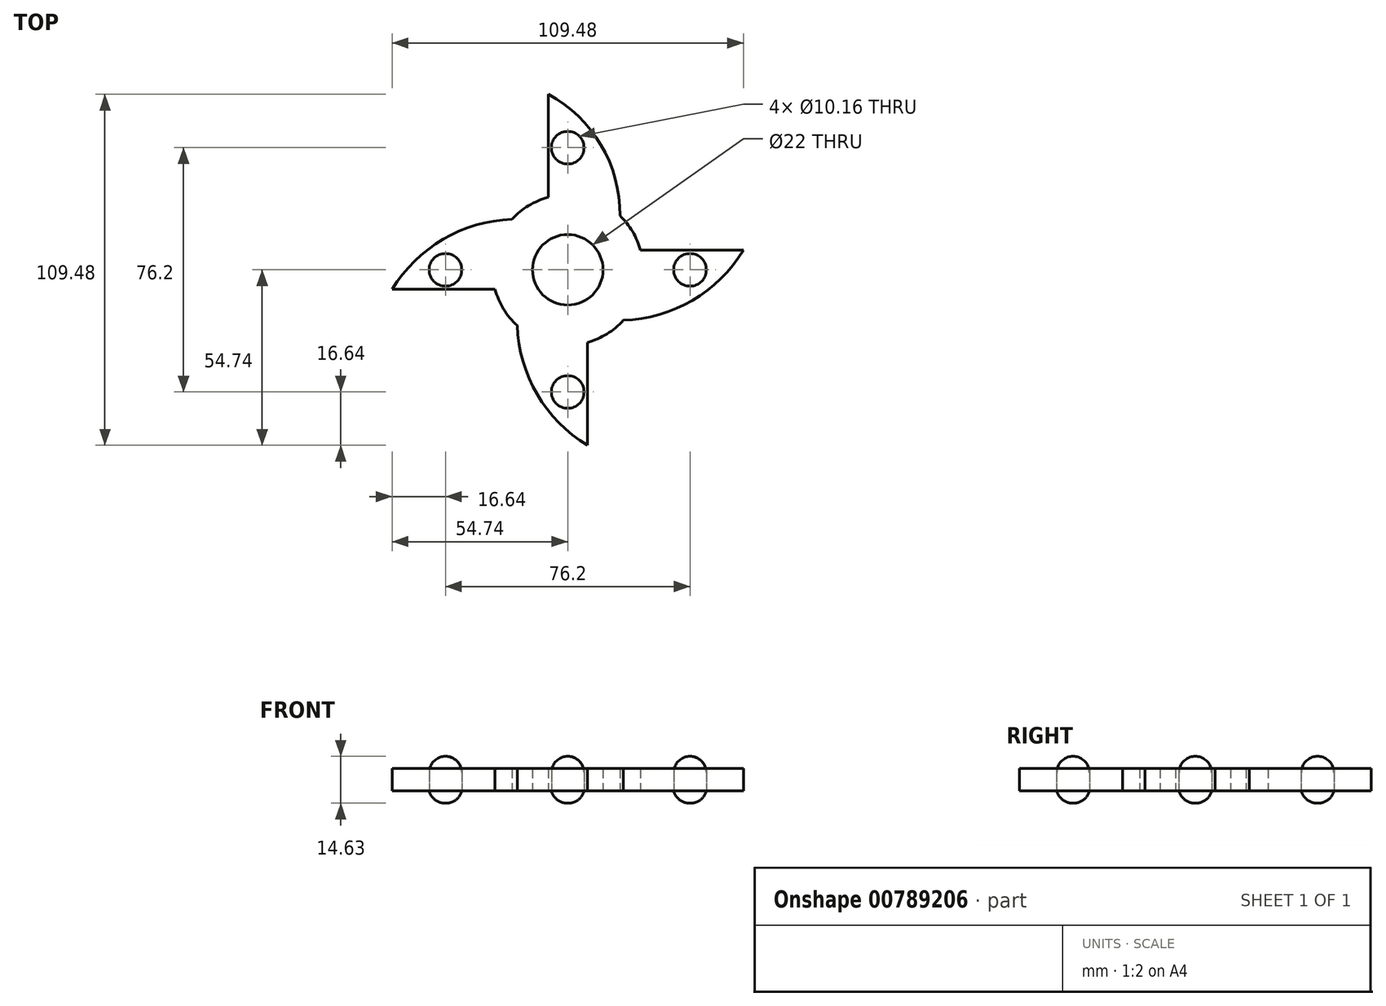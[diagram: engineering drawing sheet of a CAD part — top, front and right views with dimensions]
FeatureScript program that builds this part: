
annotation { "Feature Type Name" : "Feature", "Feature Type Description" : "" }
export const myFeature = defineFeature(function(context is Context, id is Id, definition is map)
    precondition{}
    {
        {
            var Q0;
            Q0=qCreatedBy(makeId("Top.planeOp"),FACE);
            var sketch = newSketch(context, id + "F0", { "sketchPlane" : qUnion([Q0])});
            skCircle(sketch, "E0", {"center": v(0, 0) * mm, "radius": 11 * mm});
            skCircle(sketch, "E1", {"center": v(0, 0) * mm, "radius": 4 * mm});
            skCircle(sketch, "E2", {"center": v(0, 0) * mm, "radius": 12.5 * mm});
            skCircle(sketch, "E3.cCircle", {"center": v(0, 0) * mm, "radius": 12.5 * mm, "construction": true});
            skCircle(sketch, "E4.cCircle", {"center": v(0, 0) * mm, "radius": 14.74 * mm, "construction": true});
            skLineSegment(sketch, "E4.0", {"start": v(6.1, -14.74) * mm, "end": v(-6.1, -14.74) * mm});
            skLineSegment(sketch, "E4.1", {"start": v(-6.1, -14.74) * mm, "end": v(-14.74, -6.1) * mm});
            skLineSegment(sketch, "E4.2", {"start": v(-14.74, -6.1) * mm, "end": v(-14.74, 6.1) * mm});
            skLineSegment(sketch, "E4.3", {"start": v(-14.74, 6.1) * mm, "end": v(-6.1, 14.74) * mm});
            skLineSegment(sketch, "E4.4", {"start": v(-6.1, 14.74) * mm, "end": v(6.1, 14.74) * mm});
            skLineSegment(sketch, "E4.5", {"start": v(6.1, 14.74) * mm, "end": v(14.74, 6.1) * mm});
            skLineSegment(sketch, "E4.6", {"start": v(14.74, 6.1) * mm, "end": v(14.74, -6.1) * mm});
            skLineSegment(sketch, "E4.7", {"start": v(14.74, -6.1) * mm, "end": v(6.1, -14.74) * mm});
            skPoint(sketch, "E4.0.midPoint", {"position": v(0, -14.74) * mm});
            skLineSegment(sketch, "E5", {"start": v(-6.1, 14.74) * mm, "end": v(-6.1, 54.74) * mm});
            skLineSegment(sketch, "E6", {"start": v(6.1, 14.74) * mm, "end": v(15.92, 22.8) * mm});
            skArc(sketch, "E7", {"start": v(14.74, 6.1) * mm, "mid": v(12.84, 34.07) * mm, "end": v(-6.1, 54.74) * mm});
            skLineSegment(sketch, "E8", {"start": v(14.74, 6.1) * mm, "end": v(54.74, 6.1) * mm});
            skLineSegment(sketch, "E9", {"start": v(14.74, -6.1) * mm, "end": v(23.72, -15.08) * mm});
            skArc(sketch, "E10", {"start": v(6.1, -14.74) * mm, "mid": v(33.75, -12.1) * mm, "end": v(54.74, 6.1) * mm});
            skLineSegment(sketch, "E11", {"start": v(6.1, -14.74) * mm, "end": v(6.1, -54.74) * mm});
            skLineSegment(sketch, "E12", {"start": v(-6.1, -14.74) * mm, "end": v(-15.08, -23.72) * mm});
            skArc(sketch, "E13", {"start": v(-14.74, -6.1) * mm, "mid": v(-12.1, -33.75) * mm, "end": v(6.1, -54.74) * mm});
            skLineSegment(sketch, "E14", {"start": v(-14.74, -6.1) * mm, "end": v(-54.74, -6.1) * mm});
            skLineSegment(sketch, "E15", {"start": v(-14.74, 6.1) * mm, "end": v(-23.72, 15.08) * mm});
            skArc(sketch, "E16", {"start": v(-6.1, 14.74) * mm, "mid": v(-33.75, 12.1) * mm, "end": v(-54.74, -6.1) * mm});
            skCircle(sketch, "E17", {"center": v(0, 0) * mm, "radius": 23.44 * mm});
            skLineSegment(sketch, "E18", {"start": v(0, 0) * mm, "end": v(-38.1, 0) * mm});
            skCircle(sketch, "E19", {"center": v(-38.1, 0) * mm, "radius": 5.08 * mm});
            skLineSegment(sketch, "E20", {"start": v(0, 0) * mm, "end": v(0, 38.1) * mm});
            skCircle(sketch, "E21", {"center": v(0, 38.1) * mm, "radius": 5.08 * mm});
            skLineSegment(sketch, "E22", {"start": v(0, 0) * mm, "end": v(38.1, 0) * mm});
            skCircle(sketch, "E23", {"center": v(38.1, 0) * mm, "radius": 5.08 * mm});
            skLineSegment(sketch, "E24", {"start": v(0, 0) * mm, "end": v(0, -38.1) * mm});
            skCircle(sketch, "E25", {"center": v(0, -38.1) * mm, "radius": 5.08 * mm});
            skLineSegment(sketch, "E26", {"start": v(-54.74, -6.1) * mm, "end": v(54.74, -6.1) * mm});
            skSolve(sketch);
        }
        {
            var Q0;
            {var subQ0=sQuery(id+"F0.wireOp",EDGE,"E11");var subQ5=sQuery(id+"F0.wireOp",EDGE,"E17");var subQ6=makeQuery(id+"F0.imprint","INTERSECT",VERTEX,{"derivedFrom":[subQ0,subQ5]});Q0=makeQuery(id+"F0.imprint","IMPRINT",FACE,{"disambiguationData":[TD([[makeQuery(id+"F0.imprint","IMPRINT",EDGE,{"disambiguationData":[TD([[subQ6,1.0]])],"derivedFrom":subQ5}),1.0]])]});}
            var Q1;
            {var subQ0=sQuery(id+"F0.wireOp",EDGE,"E20");var subQ1=sQuery(id+"F0.wireOp",EDGE,"E0");var subQ2=makeQuery(id+"F0.imprint","INTERSECT",VERTEX,{"derivedFrom":[subQ1,subQ0]});Q1=makeQuery(id+"F0.imprint","IMPRINT",FACE,{"disambiguationData":[TD([[makeQuery(id+"F0.imprint","IMPRINT",EDGE,{"disambiguationData":[TD([[subQ2,1.0]])],"derivedFrom":subQ1}),-1.0]])]});}
            var Q2;
            {var subQ0=sQuery(id+"F0.wireOp",EDGE,"E20");var subQ1=sQuery(id+"F0.wireOp",EDGE,"E0");var subQ2=makeQuery(id+"F0.imprint","INTERSECT",VERTEX,{"derivedFrom":[subQ1,subQ0]});Q2=makeQuery(id+"F0.imprint","IMPRINT",FACE,{"disambiguationData":[TD([[makeQuery(id+"F0.imprint","IMPRINT",EDGE,{"disambiguationData":[TD([[subQ2,-1.0]])],"derivedFrom":subQ1}),-1.0]])]});}
            var Q3;
            {var subQ0=sQuery(id+"F0.wireOp",EDGE,"E18");var subQ1=sQuery(id+"F0.wireOp",EDGE,"E0");var subQ2=makeQuery(id+"F0.imprint","INTERSECT",VERTEX,{"derivedFrom":[subQ1,subQ0]});Q3=makeQuery(id+"F0.imprint","IMPRINT",FACE,{"disambiguationData":[TD([[makeQuery(id+"F0.imprint","IMPRINT",EDGE,{"disambiguationData":[TD([[subQ2,-1.0]])],"derivedFrom":subQ1}),-1.0]])]});}
            var Q4;
            {var subQ0=sQuery(id+"F0.wireOp",EDGE,"E26");var subQ1=sQuery(id+"F0.wireOp",EDGE,"E0");var subQ2=makeQuery(id+"F0.imprint","INTERSECT",VERTEX,{"disambiguationData":[OD(0.0)],"derivedFrom":[subQ1,subQ0]});Q4=makeQuery(id+"F0.imprint","IMPRINT",FACE,{"disambiguationData":[TD([[makeQuery(id+"F0.imprint","IMPRINT",EDGE,{"disambiguationData":[TD([[subQ2,-1.0]])],"derivedFrom":subQ1}),-1.0]])]});}
            var Q5;
            {var subQ0=sQuery(id+"F0.wireOp",EDGE,"E24");var subQ1=sQuery(id+"F0.wireOp",EDGE,"E0");var subQ2=makeQuery(id+"F0.imprint","INTERSECT",VERTEX,{"derivedFrom":[subQ1,subQ0]});Q5=makeQuery(id+"F0.imprint","IMPRINT",FACE,{"disambiguationData":[TD([[makeQuery(id+"F0.imprint","IMPRINT",EDGE,{"disambiguationData":[TD([[subQ2,-1.0]])],"derivedFrom":subQ1}),-1.0]])]});}
            var Q6;
            {var subQ0=sQuery(id+"F0.wireOp",EDGE,"E22");var subQ1=sQuery(id+"F0.wireOp",EDGE,"E0");var subQ2=makeQuery(id+"F0.imprint","INTERSECT",VERTEX,{"derivedFrom":[subQ1,subQ0]});Q6=makeQuery(id+"F0.imprint","IMPRINT",FACE,{"disambiguationData":[TD([[makeQuery(id+"F0.imprint","IMPRINT",EDGE,{"disambiguationData":[TD([[subQ2,1.0]])],"derivedFrom":subQ1}),-1.0]])]});}
            var Q7;
            {var subQ0=sQuery(id+"F0.wireOp",EDGE,"E8");var subQ5=sQuery(id+"F0.wireOp",EDGE,"E17");var subQ6=makeQuery(id+"F0.imprint","INTERSECT",VERTEX,{"derivedFrom":[subQ0,subQ5]});Q7=makeQuery(id+"F0.imprint","IMPRINT",FACE,{"disambiguationData":[TD([[makeQuery(id+"F0.imprint","IMPRINT",EDGE,{"disambiguationData":[TD([[subQ6,1.0]])],"derivedFrom":subQ5}),1.0]])]});}
            var Q8;
            {var subQ3=sQuery(id+"F0.wireOp",EDGE,"E22");var subQ5=sQuery(id+"F0.wireOp",EDGE,"E17");var subQ6=makeQuery(id+"F0.imprint","INTERSECT",VERTEX,{"derivedFrom":[subQ5,subQ3]});Q8=makeQuery(id+"F0.imprint","IMPRINT",FACE,{"disambiguationData":[TD([[makeQuery(id+"F0.imprint","IMPRINT",EDGE,{"disambiguationData":[TD([[subQ6,1.0]])],"derivedFrom":subQ5}),1.0]])]});}
            var Q9;
            {var subQ0=sQuery(id+"F0.wireOp",EDGE,"E4.7");Q9=makeQuery(id+"F0.imprint","IMPRINT",FACE,{"disambiguationData":[TD([[makeQuery(id+"F0.imprint","IMPRINT",EDGE,{"derivedFrom":subQ0}),1.0]])]});}
            var Q10;
            {var subQ3=sQuery(id+"F0.wireOp",EDGE,"E18");var subQ5=sQuery(id+"F0.wireOp",EDGE,"E17");var subQ6=makeQuery(id+"F0.imprint","INTERSECT",VERTEX,{"derivedFrom":[subQ5,subQ3]});Q10=makeQuery(id+"F0.imprint","IMPRINT",FACE,{"disambiguationData":[TD([[makeQuery(id+"F0.imprint","IMPRINT",EDGE,{"disambiguationData":[TD([[subQ6,-1.0]])],"derivedFrom":subQ5}),1.0]])]});}
            var Q11;
            {var subQ3=sQuery(id+"F0.wireOp",EDGE,"E18");var subQ5=sQuery(id+"F0.wireOp",EDGE,"E17");var subQ7=makeQuery(id+"F0.imprint","INTERSECT",VERTEX,{"derivedFrom":[subQ5,subQ3]});Q11=makeQuery(id+"F0.imprint","IMPRINT",FACE,{"disambiguationData":[TD([[makeQuery(id+"F0.imprint","IMPRINT",EDGE,{"disambiguationData":[TD([[subQ7,1.0]])],"derivedFrom":subQ5}),1.0]])]});}
            var Q12;
            {var subQ0=sQuery(id+"F0.wireOp",EDGE,"E4.3");Q12=makeQuery(id+"F0.imprint","IMPRINT",FACE,{"disambiguationData":[TD([[makeQuery(id+"F0.imprint","IMPRINT",EDGE,{"derivedFrom":subQ0}),1.0]])]});}
            var Q13;
            {var subQ0=sQuery(id+"F0.wireOp",EDGE,"E18");var subQ1=sQuery(id+"F0.wireOp",EDGE,"E2");var subQ2=makeQuery(id+"F0.imprint","INTERSECT",VERTEX,{"derivedFrom":[subQ1,subQ0]});Q13=makeQuery(id+"F0.imprint","IMPRINT",FACE,{"disambiguationData":[TD([[makeQuery(id+"F0.imprint","IMPRINT",EDGE,{"disambiguationData":[TD([[subQ2,-1.0]])],"derivedFrom":subQ1}),-1.0]])]});}
            var Q14;
            {var subQ0=sQuery(id+"F0.wireOp",EDGE,"E22");var subQ1=sQuery(id+"F0.wireOp",EDGE,"E2");var subQ2=makeQuery(id+"F0.imprint","INTERSECT",VERTEX,{"derivedFrom":[subQ1,subQ0]});Q14=makeQuery(id+"F0.imprint","IMPRINT",FACE,{"disambiguationData":[TD([[makeQuery(id+"F0.imprint","IMPRINT",EDGE,{"disambiguationData":[TD([[subQ2,1.0]])],"derivedFrom":subQ1}),-1.0]])]});}
            var Q15;
            {var subQ0=sQuery(id+"F0.wireOp",EDGE,"E4.5");Q15=makeQuery(id+"F0.imprint","IMPRINT",FACE,{"disambiguationData":[TD([[makeQuery(id+"F0.imprint","IMPRINT",EDGE,{"derivedFrom":subQ0}),1.0]])]});}
            var Q16;
            {var subQ0=sQuery(id+"F0.wireOp",EDGE,"E5");var subQ5=sQuery(id+"F0.wireOp",EDGE,"E17");var subQ7=makeQuery(id+"F0.imprint","INTERSECT",VERTEX,{"derivedFrom":[subQ0,subQ5]});Q16=makeQuery(id+"F0.imprint","IMPRINT",FACE,{"disambiguationData":[TD([[makeQuery(id+"F0.imprint","IMPRINT",EDGE,{"disambiguationData":[TD([[subQ7,1.0]])],"derivedFrom":subQ5}),1.0]])]});}
            var Q17;
            {var subQ3=sQuery(id+"F0.wireOp",EDGE,"E20");var subQ5=sQuery(id+"F0.wireOp",EDGE,"E17");var subQ6=makeQuery(id+"F0.imprint","INTERSECT",VERTEX,{"derivedFrom":[subQ5,subQ3]});Q17=makeQuery(id+"F0.imprint","IMPRINT",FACE,{"disambiguationData":[TD([[makeQuery(id+"F0.imprint","IMPRINT",EDGE,{"disambiguationData":[TD([[subQ6,1.0]])],"derivedFrom":subQ5}),1.0]])]});}
            var Q18;
            Q18=makeQuery(id+"F0.imprint","IMPRINT",FACE,{"disambiguationData":[TD([[makeQuery(id+"F0.imprint","IMPRINT",EDGE,{"derivedFrom":sQuery(id+"F0.wireOp",EDGE,"E23")}),-1.0]])]});
            var Q19;
            {var subQ1=sQuery(id+"F0.wireOp",EDGE,"E10");var subQ3=sQuery(id+"F0.wireOp",EDGE,"E17");var subQ4=makeQuery(id+"F0.imprint","INTERSECT",VERTEX,{"derivedFrom":[subQ1,subQ3]});Q19=makeQuery(id+"F0.imprint","IMPRINT",FACE,{"disambiguationData":[TD([[makeQuery(id+"F0.imprint","IMPRINT",EDGE,{"disambiguationData":[TD([[subQ4,1.0]])],"derivedFrom":subQ3}),1.0]])]});}
            var Q20;
            {var subQ1=sQuery(id+"F0.wireOp",EDGE,"E13");var subQ3=sQuery(id+"F0.wireOp",EDGE,"E17");var subQ4=makeQuery(id+"F0.imprint","INTERSECT",VERTEX,{"derivedFrom":[subQ1,subQ3]});Q20=makeQuery(id+"F0.imprint","IMPRINT",FACE,{"disambiguationData":[TD([[makeQuery(id+"F0.imprint","IMPRINT",EDGE,{"disambiguationData":[TD([[subQ4,1.0]])],"derivedFrom":subQ3}),1.0]])]});}
            var Q21;
            {var subQ0=sQuery(id+"F0.wireOp",EDGE,"E13");var subQ1=sQuery(id+"F0.wireOp",EDGE,"E12");var subQ2=makeQuery(id+"F0.imprint","INTERSECT",VERTEX,{"derivedFrom":[subQ1,subQ0]});Q21=makeQuery(id+"F0.imprint","IMPRINT",FACE,{"disambiguationData":[TD([[makeQuery(id+"F0.imprint","IMPRINT",EDGE,{"disambiguationData":[TD([[subQ2,1.0]])],"derivedFrom":subQ1}),-1.0]])]});}
            var Q22;
            {var subQ1=sQuery(id+"F0.wireOp",EDGE,"E7");var subQ3=sQuery(id+"F0.wireOp",EDGE,"E17");var subQ4=makeQuery(id+"F0.imprint","INTERSECT",VERTEX,{"derivedFrom":[subQ1,subQ3]});Q22=makeQuery(id+"F0.imprint","IMPRINT",FACE,{"disambiguationData":[TD([[makeQuery(id+"F0.imprint","IMPRINT",EDGE,{"disambiguationData":[TD([[subQ4,1.0]])],"derivedFrom":subQ3}),1.0]])]});}
            var Q23;
            {var subQ0=sQuery(id+"F0.wireOp",EDGE,"E10");var subQ1=sQuery(id+"F0.wireOp",EDGE,"E9");var subQ2=makeQuery(id+"F0.imprint","INTERSECT",VERTEX,{"derivedFrom":[subQ1,subQ0]});Q23=makeQuery(id+"F0.imprint","IMPRINT",FACE,{"disambiguationData":[TD([[makeQuery(id+"F0.imprint","IMPRINT",EDGE,{"disambiguationData":[TD([[subQ2,1.0]])],"derivedFrom":subQ1}),-1.0]])]});}
            var Q24;
            {var subQ1=sQuery(id+"F0.wireOp",EDGE,"E5");var subQ3=sQuery(id+"F0.wireOp",EDGE,"E17");var subQ4=makeQuery(id+"F0.imprint","INTERSECT",VERTEX,{"derivedFrom":[subQ1,subQ3]});Q24=makeQuery(id+"F0.imprint","IMPRINT",FACE,{"disambiguationData":[TD([[makeQuery(id+"F0.imprint","IMPRINT",EDGE,{"disambiguationData":[TD([[subQ4,-1.0]])],"derivedFrom":subQ3}),1.0]])]});}
            var Q25;
            {var subQ0=sQuery(id+"F0.wireOp",EDGE,"E16");var subQ1=sQuery(id+"F0.wireOp",EDGE,"E15");var subQ2=makeQuery(id+"F0.imprint","INTERSECT",VERTEX,{"derivedFrom":[subQ1,subQ0]});Q25=makeQuery(id+"F0.imprint","IMPRINT",FACE,{"disambiguationData":[TD([[makeQuery(id+"F0.imprint","IMPRINT",EDGE,{"disambiguationData":[TD([[subQ2,1.0]])],"derivedFrom":subQ1}),-1.0]])]});}
            var Q26;
            Q26=makeQuery(id+"F0.imprint","IMPRINT",FACE,{"disambiguationData":[TD([[makeQuery(id+"F0.imprint","IMPRINT",EDGE,{"derivedFrom":sQuery(id+"F0.wireOp",EDGE,"E21")}),-1.0]])]});
            var Q27;
            {var subQ0=sQuery(id+"F0.wireOp",EDGE,"E7");var subQ1=sQuery(id+"F0.wireOp",EDGE,"E6");var subQ2=makeQuery(id+"F0.imprint","INTERSECT",VERTEX,{"derivedFrom":[subQ1,subQ0]});Q27=makeQuery(id+"F0.imprint","IMPRINT",FACE,{"disambiguationData":[TD([[makeQuery(id+"F0.imprint","IMPRINT",EDGE,{"disambiguationData":[TD([[subQ2,1.0]])],"derivedFrom":subQ1}),-1.0]])]});}
            var Q28;
            {var subQ0=sQuery(id+"F0.wireOp",EDGE,"E4.1");Q28=makeQuery(id+"F0.imprint","IMPRINT",FACE,{"disambiguationData":[TD([[makeQuery(id+"F0.imprint","IMPRINT",EDGE,{"derivedFrom":subQ0}),1.0]])]});}
            var Q29;
            {var subQ3=sQuery(id+"F0.wireOp",EDGE,"E24");var subQ5=sQuery(id+"F0.wireOp",EDGE,"E17");var subQ7=makeQuery(id+"F0.imprint","INTERSECT",VERTEX,{"derivedFrom":[subQ5,subQ3]});Q29=makeQuery(id+"F0.imprint","IMPRINT",FACE,{"disambiguationData":[TD([[makeQuery(id+"F0.imprint","IMPRINT",EDGE,{"disambiguationData":[TD([[subQ7,1.0]])],"derivedFrom":subQ5}),1.0]])]});}
            var Q30;
            {var subQ0=sQuery(id+"F0.wireOp",EDGE,"E4.7");Q30=makeQuery(id+"F0.imprint","IMPRINT",FACE,{"disambiguationData":[TD([[makeQuery(id+"F0.imprint","IMPRINT",EDGE,{"derivedFrom":subQ0}),-1.0]])]});}
            var Q31;
            {var subQ0=sQuery(id+"F0.wireOp",EDGE,"E4.5");Q31=makeQuery(id+"F0.imprint","IMPRINT",FACE,{"disambiguationData":[TD([[makeQuery(id+"F0.imprint","IMPRINT",EDGE,{"derivedFrom":subQ0}),-1.0]])]});}
            var Q32;
            {var subQ5=sQuery(id+"F0.wireOp",EDGE,"E4.1");Q32=makeQuery(id+"F0.imprint","IMPRINT",FACE,{"disambiguationData":[TD([[makeQuery(id+"F0.imprint","IMPRINT",EDGE,{"derivedFrom":subQ5}),-1.0]])]});}
            var Q33;
            {var subQ1=sQuery(id+"F0.wireOp",EDGE,"E4.3");Q33=makeQuery(id+"F0.imprint","IMPRINT",FACE,{"disambiguationData":[TD([[makeQuery(id+"F0.imprint","IMPRINT",EDGE,{"derivedFrom":subQ1}),-1.0]])]});}
            var Q34;
            {var subQ0=sQuery(id+"F0.wireOp",EDGE,"E10");var subQ1=sQuery(id+"F0.wireOp",EDGE,"E9");var subQ2=makeQuery(id+"F0.imprint","INTERSECT",VERTEX,{"derivedFrom":[subQ1,subQ0]});Q34=makeQuery(id+"F0.imprint","IMPRINT",FACE,{"disambiguationData":[TD([[makeQuery(id+"F0.imprint","IMPRINT",EDGE,{"disambiguationData":[TD([[subQ2,1.0]])],"derivedFrom":subQ1}),1.0]])]});}
            var Q35;
            Q35=makeQuery(id+"F0.imprint","IMPRINT",FACE,{"disambiguationData":[TD([[makeQuery(id+"F0.imprint","IMPRINT",EDGE,{"derivedFrom":sQuery(id+"F0.wireOp",EDGE,"E25")}),-1.0]])]});
            var Q36;
            Q36=makeQuery(id+"F0.imprint","IMPRINT",FACE,{"disambiguationData":[TD([[makeQuery(id+"F0.imprint","IMPRINT",EDGE,{"derivedFrom":sQuery(id+"F0.wireOp",EDGE,"E19")}),-1.0]])]});
            var Q37;
            {var subQ1=sQuery(id+"F0.wireOp",EDGE,"E9");var subQ3=sQuery(id+"F0.wireOp",EDGE,"E17");var subQ4=makeQuery(id+"F0.imprint","INTERSECT",VERTEX,{"derivedFrom":[subQ1,subQ3]});Q37=makeQuery(id+"F0.imprint","IMPRINT",FACE,{"disambiguationData":[TD([[makeQuery(id+"F0.imprint","IMPRINT",EDGE,{"disambiguationData":[TD([[subQ4,-1.0]])],"derivedFrom":subQ3}),1.0]])]});}
            extrude(context, id + "F1", {"entities" : qUnion([Q0, Q1, Q2, Q3, Q4, Q5, Q6, Q7, Q8, Q9, Q10, Q11, Q12, Q13, Q14, Q15, Q16, Q17, Q18, Q19, Q20, Q21, Q22, Q23, Q24, Q25, Q26, Q27, Q28, Q29, Q30, Q31, Q32, Q33, Q34, Q35, Q36, Q37]), "depth" : 7 * mm, "offsetDistance" : 25.4 * mm});
        }
        {
            var Q0;
            Q0=makeQuery(id+"F0.imprint","IMPRINT",FACE,{"disambiguationData":[TD([[makeQuery(id+"F0.imprint","IMPRINT",EDGE,{"derivedFrom":sQuery(id+"F0.wireOp",EDGE,"E25")}),1.0]])]});
            var sketch = newSketch(context, id + "F2", { "sketchPlane" : qUnion([Q0])});
            skSolve(sketch);
        }
        {
            var Q0;
            Q0 = qSketchRegion(id + "F2", true);
            var Q1;
            Q1=makeQuery(id+"F0.imprint","IMPRINT",FACE,{"disambiguationData":[TD([[makeQuery(id+"F0.imprint","IMPRINT",EDGE,{"derivedFrom":sQuery(id+"F0.wireOp",EDGE,"E25")}),1.0]])]});
            extrude(context, id + "F3", {"entities" : qUnion([Q0, Q1]), "depth" : -3.8 * mm, "offsetDistance" : 25.4 * mm});
        }
        {
            var Q0;
            Q0=makeQuery(id+"F3.opExtrude","CAP_EDGE",EDGE,{"disambiguationData":[OSD([sQuery(id+"F0.wireOp",EDGE,"E25")])],"isStart":false});
            fillet(context, id + "F4", {"entities" : qUnion([Q0]), "radius" : 5.08 * mm, "tangentPropagation" : true, "allowEdgeOverflow" : false});
        }
        {
            var Q0;
            Q0=makeQuery(id+"F0.imprint","IMPRINT",FACE,{"disambiguationData":[TD([[makeQuery(id+"F0.imprint","IMPRINT",EDGE,{"derivedFrom":sQuery(id+"F0.wireOp",EDGE,"E25")}),1.0]])]});
            extrude(context, id + "F5", {"entities" : qUnion([Q0]), "depth" : 10.82 * mm, "offsetDistance" : 25.4 * mm});
        }
        {
            var Q0;
            Q0=makeQuery(id+"F5.opExtrude","CAP_FACE",FACE,{"disambiguationData":[OSD([sQuery(id+"F0.wireOp",EDGE,"E25")])],"isStart":false});
            fillet(context, id + "F6", {"entities" : qUnion([Q0]), "radius" : 5.08 * mm, "tangentPropagation" : true, "allowEdgeOverflow" : false});
        }
        {
            var Q0;
            Q0=makeQuery(id+"F0.imprint","IMPRINT",FACE,{"disambiguationData":[TD([[makeQuery(id+"F0.imprint","IMPRINT",EDGE,{"derivedFrom":sQuery(id+"F0.wireOp",EDGE,"E19")}),1.0]])]});
            extrude(context, id + "F7", {"entities" : qUnion([Q0]), "depth" : -3.8 * mm, "offsetDistance" : 25.4 * mm});
        }
        {
            var Q0;
            Q0=makeQuery(id+"F7.opExtrude","CAP_FACE",FACE,{"disambiguationData":[OSD([sQuery(id+"F0.wireOp",EDGE,"E19")])],"isStart":false});
            fillet(context, id + "F8", {"entities" : qUnion([Q0]), "radius" : 5.08 * mm, "tangentPropagation" : true, "allowEdgeOverflow" : false});
        }
        {
            var Q0;
            Q0=makeQuery(id+"F0.imprint","IMPRINT",FACE,{"disambiguationData":[TD([[makeQuery(id+"F0.imprint","IMPRINT",EDGE,{"derivedFrom":sQuery(id+"F0.wireOp",EDGE,"E19")}),1.0]])]});
            extrude(context, id + "F9", {"entities" : qUnion([Q0]), "depth" : 10.82 * mm, "offsetDistance" : 25.4 * mm});
        }
        {
            var Q0;
            Q0=makeQuery(id+"F9.opExtrude","CAP_FACE",FACE,{"disambiguationData":[OSD([sQuery(id+"F0.wireOp",EDGE,"E19")])],"isStart":false});
            fillet(context, id + "F10", {"entities" : qUnion([Q0]), "radius" : 5.08 * mm, "tangentPropagation" : true, "allowEdgeOverflow" : false});
        }
        {
            var Q0;
            Q0=makeQuery(id+"F0.imprint","IMPRINT",FACE,{"disambiguationData":[TD([[makeQuery(id+"F0.imprint","IMPRINT",EDGE,{"derivedFrom":sQuery(id+"F0.wireOp",EDGE,"E23")}),1.0]])]});
            extrude(context, id + "F11", {"entities" : qUnion([Q0]), "depth" : -3.8 * mm, "offsetDistance" : 25.4 * mm});
        }
        {
            var Q0;
            Q0=makeQuery(id+"F11.opExtrude","CAP_FACE",FACE,{"disambiguationData":[OSD([sQuery(id+"F0.wireOp",EDGE,"E23")])],"isStart":false});
            fillet(context, id + "F12", {"entities" : qUnion([Q0]), "radius" : 5.08 * mm, "tangentPropagation" : true, "allowEdgeOverflow" : false});
        }
        {
            var Q0;
            Q0=makeQuery(id+"F0.imprint","IMPRINT",FACE,{"disambiguationData":[TD([[makeQuery(id+"F0.imprint","IMPRINT",EDGE,{"derivedFrom":sQuery(id+"F0.wireOp",EDGE,"E23")}),1.0]])]});
            extrude(context, id + "F13", {"entities" : qUnion([Q0]), "depth" : 10.82 * mm, "offsetDistance" : 25.4 * mm});
        }
        {
            var Q0;
            Q0=makeQuery(id+"F13.opExtrude","CAP_FACE",FACE,{"disambiguationData":[OSD([sQuery(id+"F0.wireOp",EDGE,"E23")])],"isStart":false});
            fillet(context, id + "F14", {"entities" : qUnion([Q0]), "radius" : 5.08 * mm, "tangentPropagation" : true, "allowEdgeOverflow" : false});
        }
        {
            var Q0;
            Q0=makeQuery(id+"F0.imprint","IMPRINT",FACE,{"disambiguationData":[TD([[makeQuery(id+"F0.imprint","IMPRINT",EDGE,{"derivedFrom":sQuery(id+"F0.wireOp",EDGE,"E21")}),1.0]])]});
            extrude(context, id + "F15", {"entities" : qUnion([Q0]), "depth" : -3.8 * mm, "offsetDistance" : 25.4 * mm});
        }
        {
            var Q0;
            Q0=makeQuery(id+"F15.opExtrude","CAP_FACE",FACE,{"disambiguationData":[OSD([sQuery(id+"F0.wireOp",EDGE,"E21")])],"isStart":false});
            fillet(context, id + "F16", {"entities" : qUnion([Q0]), "radius" : 5.08 * mm, "tangentPropagation" : true, "allowEdgeOverflow" : false});
        }
        {
            var Q0;
            Q0=makeQuery(id+"F0.imprint","IMPRINT",FACE,{"disambiguationData":[TD([[makeQuery(id+"F0.imprint","IMPRINT",EDGE,{"derivedFrom":sQuery(id+"F0.wireOp",EDGE,"E21")}),1.0]])]});
            extrude(context, id + "F17", {"entities" : qUnion([Q0]), "depth" : 10.82 * mm, "offsetDistance" : 25.4 * mm});
        }
        {
            var Q0;
            Q0=makeQuery(id+"F17.opExtrude","CAP_FACE",FACE,{"disambiguationData":[OSD([sQuery(id+"F0.wireOp",EDGE,"E21")])],"isStart":false});
            fillet(context, id + "F18", {"entities" : qUnion([Q0]), "radius" : 5.08 * mm, "tangentPropagation" : true, "allowEdgeOverflow" : false});
        }
    });
